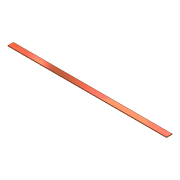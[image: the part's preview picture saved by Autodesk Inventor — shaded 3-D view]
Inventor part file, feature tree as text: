
AUTODESK INVENTOR PART (.ipt)
format: ipt  version: 2012 (Build 160160000, 160)  size: 69,120 bytes
history: native  units: in
note: dims shown in document units (in); Inventor stores cm internally (conversion verified against a paired STEP export)
features: extrude x1, sketch x1
ambient origin geometry x8: Origin, YZ Plane, XZ Plane, XY Plane, X Axis, Y Axis, Z Axis, Center Point
bodies: Solid1 (feature_tree)
feature tree (2):
  extrude  "Extrusion1"  Depth=344.1395in
  sketch  "Sketch1"  dims[d0=1.5in d1=344.1395in d2=12.0in d3=0.0in]
